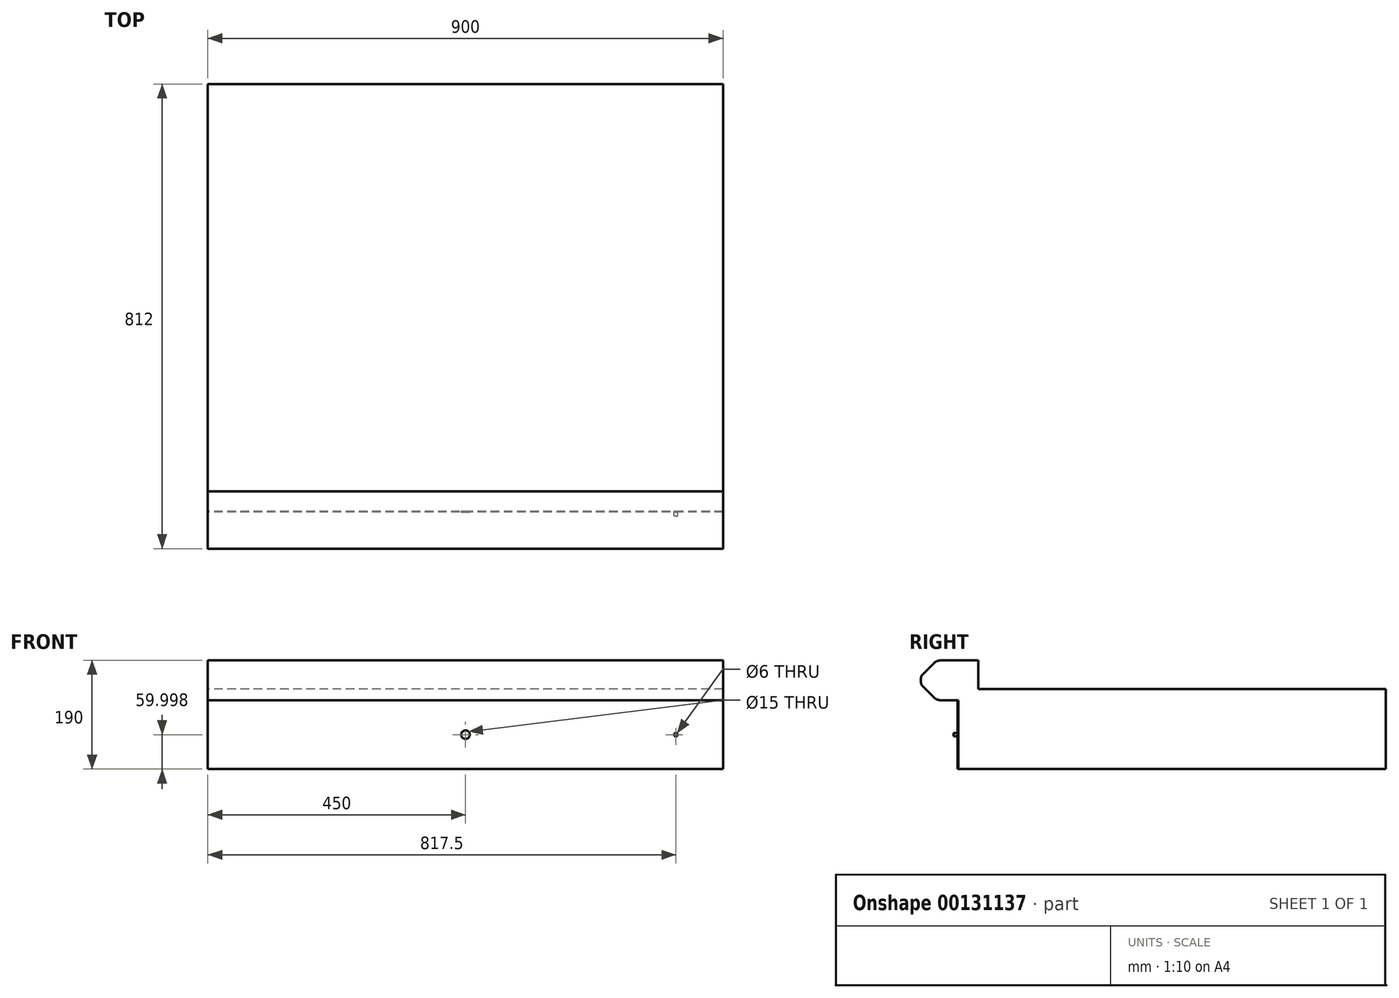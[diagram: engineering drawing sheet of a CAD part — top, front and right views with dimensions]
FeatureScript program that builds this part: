
annotation { "Feature Type Name" : "Feature", "Feature Type Description" : "" }
export const myFeature = defineFeature(function(context is Context, id is Id, definition is map)
    precondition{}
    {
        {
            var Q0;
            Q0=qCreatedBy(makeId("Right.planeOp"),FACE);
            var sketch = newSketch(context, id + "F0", { "sketchPlane" : qUnion([Q0])});
            skLineSegment(sketch, "E0.bottom", {"start": v(-402.8, 333.65) * mm, "end": v(-332.8, 333.65) * mm});
            skLineSegment(sketch, "E0.top", {"start": v(-402.8, 553.65) * mm, "end": v(-332.8, 553.65) * mm});
            skLineSegment(sketch, "E0.left", {"start": v(-402.8, 333.65) * mm, "end": v(-402.8, 553.65) * mm});
            skLineSegment(sketch, "E0.right", {"start": v(-332.8, 333.65) * mm, "end": v(-332.8, 553.65) * mm});
            skLineSegment(sketch, "E1", {"start": v(-332.8, 333.65) * mm, "end": v(-1044.8, 333.65) * mm});
            skPoint(sketch, "E1.endSnap0", {"position": v(-367.8, 333.65) * mm});
            skLineSegment(sketch, "E2", {"start": v(-1044.8, 333.65) * mm, "end": v(-1044.8, 383.65) * mm});
            skLineSegment(sketch, "E3", {"start": v(-1044.8, 383.65) * mm, "end": v(-1144.8, 383.65) * mm});
            skLineSegment(sketch, "E4", {"start": v(-1144.8, 383.65) * mm, "end": v(-1144.8, 313.65) * mm});
            skLineSegment(sketch, "E5", {"start": v(-1144.8, 313.65) * mm, "end": v(-1079.8, 313.65) * mm});
            skLineSegment(sketch, "E6", {"start": v(-1079.8, 313.65) * mm, "end": v(-1079.8, 193.65) * mm});
            skLineSegment(sketch, "E7", {"start": v(-1079.8, 193.65) * mm, "end": v(-332.8, 193.65) * mm});
            skLineSegment(sketch, "E8", {"start": v(-332.8, 193.65) * mm, "end": v(-332.8, 333.65) * mm});
            skLineSegment(sketch, "E9.bottom", {"start": v(-332.8, 193.65) * mm, "end": v(-1029.8, 193.65) * mm});
            skLineSegment(sketch, "E9.top", {"start": v(-332.8, -381.35) * mm, "end": v(-1029.8, -381.35) * mm});
            skLineSegment(sketch, "E9.left", {"start": v(-332.8, 193.65) * mm, "end": v(-332.8, -381.35) * mm});
            skLineSegment(sketch, "E9.right", {"start": v(-1029.8, 193.65) * mm, "end": v(-1029.8, -381.35) * mm});
            skLineSegment(sketch, "E10", {"start": v(-1029.8, -381.35) * mm, "end": v(-1029.8, -311.35) * mm});
            skLineSegment(sketch, "E11", {"start": v(-1029.8, -311.35) * mm, "end": v(-1079.8, -311.35) * mm});
            skLineSegment(sketch, "E12", {"start": v(-1079.8, -311.35) * mm, "end": v(-1079.8, -341.35) * mm});
            skLineSegment(sketch, "E13", {"start": v(-1079.8, -341.35) * mm, "end": v(-1049.8, -381.35) * mm});
            skLineSegment(sketch, "E14", {"start": v(-1049.8, -381.35) * mm, "end": v(-1029.8, -381.35) * mm});
            skLineSegment(sketch, "E15", {"start": v(-1029.8, 183.65) * mm, "end": v(-1076.8, 183.65) * mm});
            skLineSegment(sketch, "E16", {"start": v(-1079.35, 179.07) * mm, "end": v(-1069.8, 163.65) * mm});
            skLineSegment(sketch, "E17", {"start": v(-1069.8, 163.65) * mm, "end": v(-1029.8, 163.65) * mm});
            skLineSegment(sketch, "E18", {"start": v(-1029.8, 163.65) * mm, "end": v(-1029.8, 183.65) * mm});
            skPoint(sketch, "E19.visualSharp", {"position": v(-1082.19, 183.65) * mm});
            skArc(sketch, "E19.filletArc", {"start": v(-1076.8, 183.65) * mm, "mid": v(-1079.42, 182.1) * mm, "end": v(-1079.35, 179.07) * mm});
            skLineSegment(sketch, "E20", {"start": v(-1079.8, -301.35) * mm, "end": v(-1029.8, -301.35) * mm});
            skLineSegment(sketch, "E21", {"start": v(-1029.8, -301.35) * mm, "end": v(-1029.8, 153.65) * mm});
            skLineSegment(sketch, "E22", {"start": v(-1029.8, 153.65) * mm, "end": v(-1049.8, 153.65) * mm});
            skLineSegment(sketch, "E23", {"start": v(-1049.8, 153.65) * mm, "end": v(-1079.8, 113.65) * mm});
            skLineSegment(sketch, "E24", {"start": v(-1079.8, 113.65) * mm, "end": v(-1079.8, -301.35) * mm});
            skSolve(sketch);
        }
        {
            var Q0;
            {var subQ0=sQuery(id+"F0.wireOp",EDGE,"E2");Q0=makeQuery(id+"F0.imprint","IMPRINT",FACE,{"disambiguationData":[TD([[makeQuery(id+"F0.imprint","IMPRINT",EDGE,{"derivedFrom":subQ0}),1.0]])]});}
            extrude(context, id + "F1", {"entities" : qUnion([Q0]), "depth" : 900 * mm});
        }
        {
            var Q0;
            Q0=makeQuery(id+"F1.opExtrude","SWEPT_EDGE",EDGE,{"disambiguationData":[OSD([sQuery(id+"F0.wireOp",EDGE,"E3"),sQuery(id+"F0.wireOp",EDGE,"E4")])]});
            var Q1;
            Q1=makeQuery(id+"F1.opExtrude","SWEPT_EDGE",EDGE,{"disambiguationData":[OSD([sQuery(id+"F0.wireOp",EDGE,"E4"),sQuery(id+"F0.wireOp",EDGE,"E5")])]});
            chamfer(context, id + "F2", {"entities" : qUnion([Q0, Q1]), "width" : 27.5 * mm, "tangentPropagation" : true});
        }
        {
            var Q0;
            {var subQ0=sQuery(id+"F0.wireOp",EDGE,"E3");Q0=makeQuery(id+"F2.opChamfer","BLEND_EDGE",EDGE,{"blendedFrom":[makeQuery(id+"F1.opExtrude","SWEPT_EDGE",EDGE,{"disambiguationData":[OSD([subQ0,sQuery(id+"F0.wireOp",EDGE,"E4")])]}),makeQuery(id+"F1.opExtrude","SWEPT_FACE",FACE,{"disambiguationData":[OSD([subQ0])]})],"blendedInto":[makeQuery(id+"F1.opExtrude","SWEPT_FACE",FACE,{"disambiguationData":[OSD([subQ0])]})]});}
            var Q1;
            {var subQ0=sQuery(id+"F0.wireOp",EDGE,"E5");Q1=makeQuery(id+"F2.opChamfer","BLEND_EDGE",EDGE,{"blendedFrom":[makeQuery(id+"F1.opExtrude","SWEPT_EDGE",EDGE,{"disambiguationData":[OSD([sQuery(id+"F0.wireOp",EDGE,"E4"),subQ0])]}),makeQuery(id+"F1.opExtrude","SWEPT_FACE",FACE,{"disambiguationData":[OSD([subQ0])]})],"blendedInto":[makeQuery(id+"F1.opExtrude","SWEPT_FACE",FACE,{"disambiguationData":[OSD([subQ0])]})]});}
            fillet(context, id + "F3", {"entities" : qUnion([Q0, Q1]), "radius" : 20 * mm, "tangentPropagation" : true, "allowEdgeOverflow" : false});
        }
        {
            var Q0;
            {var subQ0=sQuery(id+"F0.wireOp",EDGE,"E4");Q0=makeQuery(id+"F2.opChamfer","BLEND_EDGE",EDGE,{"blendedFrom":[makeQuery(id+"F1.opExtrude","SWEPT_EDGE",EDGE,{"disambiguationData":[OSD([sQuery(id+"F0.wireOp",EDGE,"E3"),subQ0])]}),makeQuery(id+"F1.opExtrude","SWEPT_FACE",FACE,{"disambiguationData":[OSD([subQ0])]})],"blendedInto":[makeQuery(id+"F1.opExtrude","SWEPT_FACE",FACE,{"disambiguationData":[OSD([subQ0])]})]});}
            var Q1;
            {var subQ0=sQuery(id+"F0.wireOp",EDGE,"E4");Q1=makeQuery(id+"F2.opChamfer","BLEND_EDGE",EDGE,{"blendedFrom":[makeQuery(id+"F1.opExtrude","SWEPT_EDGE",EDGE,{"disambiguationData":[OSD([subQ0,sQuery(id+"F0.wireOp",EDGE,"E5")])]}),makeQuery(id+"F1.opExtrude","SWEPT_FACE",FACE,{"disambiguationData":[OSD([subQ0])]})],"blendedInto":[makeQuery(id+"F1.opExtrude","SWEPT_FACE",FACE,{"disambiguationData":[OSD([subQ0])]})]});}
            fillet(context, id + "F4", {"entities" : qUnion([Q0, Q1]), "radius" : 10 * mm, "tangentPropagation" : true, "allowEdgeOverflow" : false});
        }
        {
            var Q0;
            Q0=makeQuery(id+"F1.opExtrude","SWEPT_FACE",FACE,{"disambiguationData":[OSD([sQuery(id+"F0.wireOp",EDGE,"E6")])]});
            var sketch = newSketch(context, id + "F5", { "sketchPlane" : qUnion([Q0])});
            skCircle(sketch, "E25", {"center": v(817.5, 253.65) * mm, "radius": 3 * mm});
            skPoint(sketch, "E25.centerSnap0", {"position": v(900, 253.65) * mm});
            skSolve(sketch);
        }
        {
            var Q0;
            Q0 = qSketchRegion(id + "F5", true);
            extrude(context, id + "F6", {"entities" : qUnion([Q0]), "operationType" : NewBodyOperationType.ADD, "depth" : 8 * mm});
        }
        {
            var Q0;
            Q0=makeQuery(id+"F1.opExtrude","SWEPT_FACE",FACE,{"disambiguationData":[OSD([sQuery(id+"F0.wireOp",EDGE,"E6")])]});
            extrude(context, id + "F7", {"entities" : qUnion([Q0]), "depth" : 1 * mm});
        }
        {
            var Q0;
            Q0=makeQuery(id+"F7.opExtrude","CAP_FACE",FACE,{"disambiguationData":[OSD([sQuery(id+"F0.wireOp",EDGE,"E6")])],"isStart":false});
            var sketch = newSketch(context, id + "F8", { "sketchPlane" : qUnion([Q0])});
            skCircle(sketch, "E26", {"center": v(450, 253.65) * mm, "radius": 7.5 * mm});
            skPoint(sketch, "E26.centerSnap0", {"position": v(0, 253.65) * mm});
            skPoint(sketch, "E26.centerSnap1", {"position": v(450, 193.65) * mm});
            skSolve(sketch);
        }
        {
            var Q0;
            Q0 = qSketchRegion(id + "F8", true);
            extrude(context, id + "F9", {"entities" : qUnion([Q0]), "operationType" : NewBodyOperationType.REMOVE, "oppositeDirection" : true, "depth" : 1 * mm});
        }
    });
